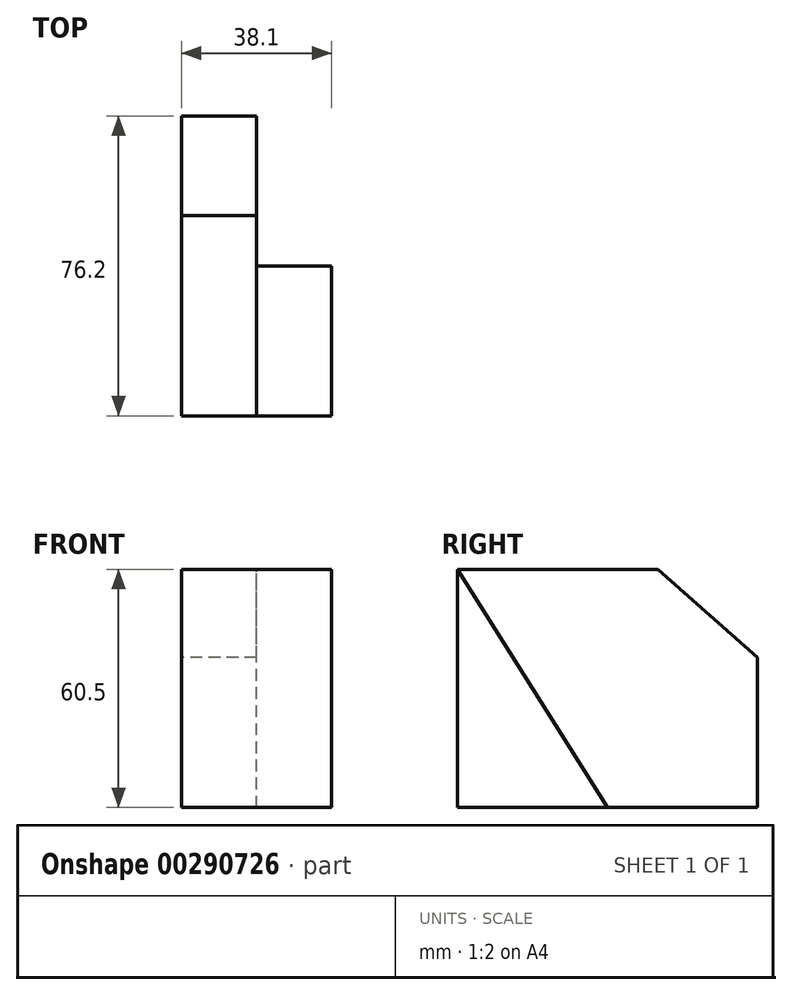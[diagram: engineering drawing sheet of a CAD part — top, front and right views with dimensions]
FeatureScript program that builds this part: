
annotation { "Feature Type Name" : "Feature", "Feature Type Description" : "" }
export const myFeature = defineFeature(function(context is Context, id is Id, definition is map)
    precondition{}
    {
        {
            var Q0;
            Q0=qCreatedBy(makeId("Right.planeOp"),FACE);
            var sketch = newSketch(context, id + "F0", { "sketchPlane" : qUnion([Q0])});
            skLineSegment(sketch, "E0", {"start": v(0, 0) * mm, "end": v(76.2, 0) * mm});
            skLineSegment(sketch, "E1", {"start": v(76.2, 0) * mm, "end": v(76.2, 38.1) * mm});
            skLineSegment(sketch, "E2", {"start": v(76.2, 38.1) * mm, "end": v(50.9, 60.5) * mm});
            skLineSegment(sketch, "E3", {"start": v(50.9, 60.5) * mm, "end": v(0, 60.5) * mm});
            skLineSegment(sketch, "E4", {"start": v(0, 60.5) * mm, "end": v(0, 0) * mm});
            skSolve(sketch);
        }
        {
            var Q0;
            Q0=makeQuery(id+"F0.imprint","IMPRINT",FACE,{"disambiguationData":[TD([[makeQuery(id+"F0.imprint","IMPRINT",EDGE,{"derivedFrom":sQuery(id+"F0.wireOp",EDGE,"E0")}),1.0]])]});
            extrude(context, id + "F1", {"entities" : qUnion([Q0]), "depth" : 19.05 * mm});
        }
        {
            var Q0;
            Q0=makeQuery(id+"F1.opExtrude","CAP_FACE",FACE,{"disambiguationData":[OSD([sQuery(id+"F0.wireOp",EDGE,"E0"),sQuery(id+"F0.wireOp",EDGE,"E1"),sQuery(id+"F0.wireOp",EDGE,"E2"),sQuery(id+"F0.wireOp",EDGE,"E3"),sQuery(id+"F0.wireOp",EDGE,"E4")])],"isStart":false});
            var sketch = newSketch(context, id + "F2", { "sketchPlane" : qUnion([Q0])});
            skLineSegment(sketch, "E5", {"start": v(38.1, 0) * mm, "end": v(0, 60.5) * mm});
            skLineSegment(sketch, "E6", {"start": v(0, 60.5) * mm, "end": v(0, 0) * mm});
            skLineSegment(sketch, "E7", {"start": v(0, 0) * mm, "end": v(38.1, 0) * mm});
            skSolve(sketch);
        }
        {
            var Q0;
            Q0=makeQuery(id+"F2.imprint","IMPRINT",FACE,{"disambiguationData":[TD([[makeQuery(id+"F2.imprint","IMPRINT",EDGE,{"derivedFrom":sQuery(id+"F2.wireOp",EDGE,"E5")}),1.0]])]});
            extrude(context, id + "F3", {"entities" : qUnion([Q0]), "operationType" : NewBodyOperationType.ADD, "depth" : 19.05 * mm});
        }
    });
